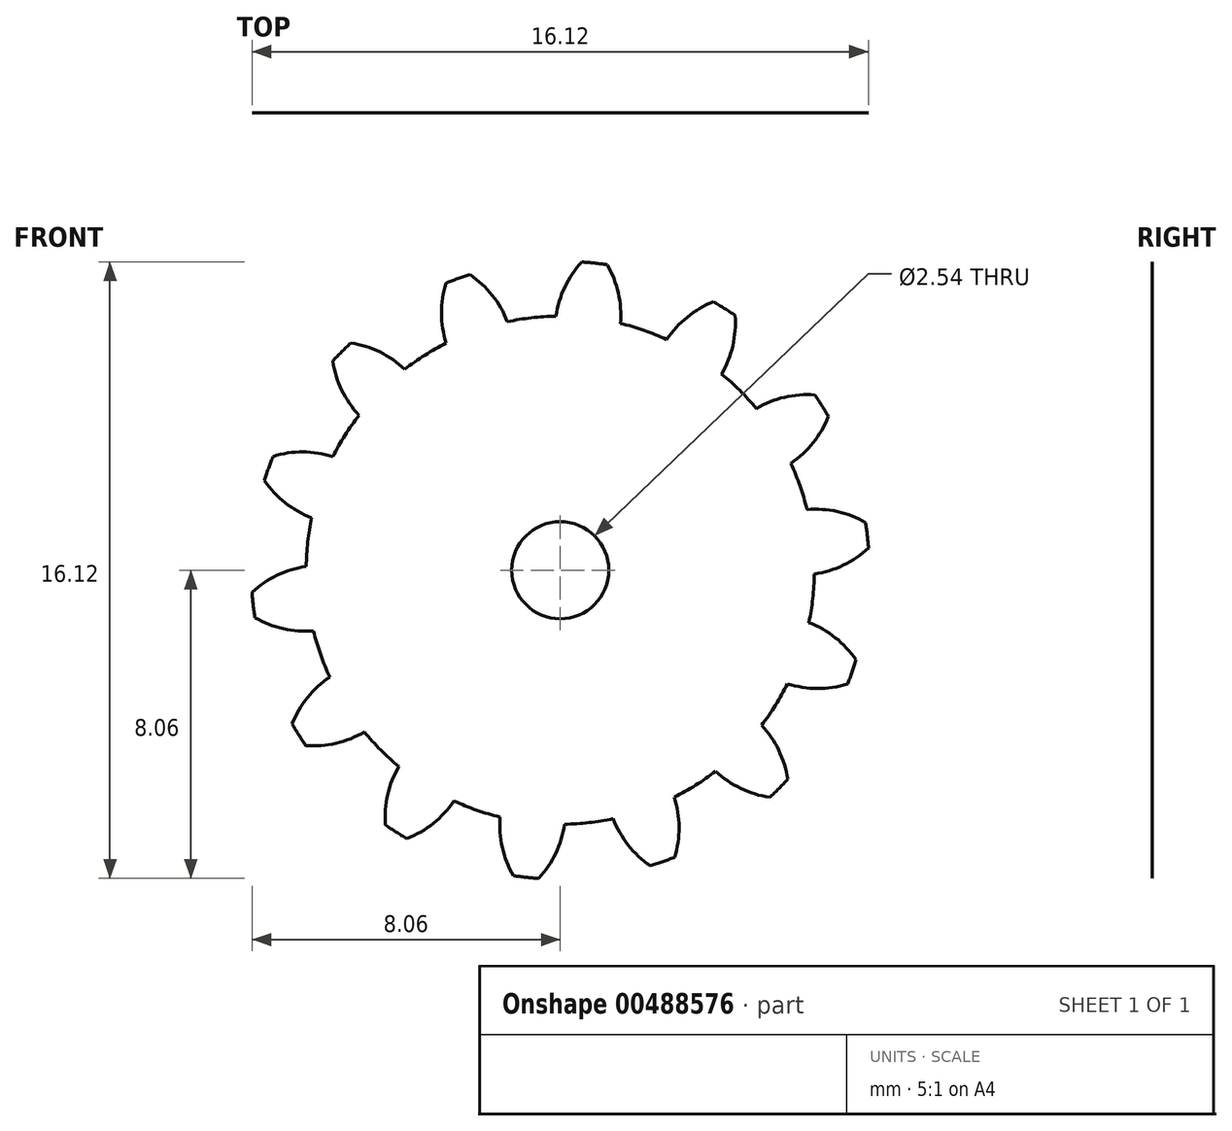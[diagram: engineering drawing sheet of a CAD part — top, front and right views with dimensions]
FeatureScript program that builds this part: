
annotation { "Feature Type Name" : "Feature", "Feature Type Description" : "" }
export const myFeature = defineFeature(function(context is Context, id is Id, definition is map)
    precondition{}
    {
        {
            assignVariable(context, id + "F0", {"name" : "teeth", "anyValue" : 14});
        }
        {
            var Q0;
            Q0=qCreatedBy(makeId("Front.planeOp"),FACE);
            var sketch = newSketch(context, id + "F1", { "sketchPlane" : qUnion([Q0])});
            skCircle(sketch, "E0", {"center": v(0, 0) * mm, "radius": 7.07 * mm, "construction": true});
            skCircle(sketch, "E1", {"center": v(0, 0) * mm, "radius": 8.08 * mm, "construction": true});
            skCircle(sketch, "E2", {"center": v(0, 0) * mm, "radius": 6.64 * mm});
            skCircle(sketch, "E3", {"center": v(14.14, 0) * mm, "radius": 6.64 * mm, "construction": true});
            skLineSegment(sketch, "E4", {"start": v(6.24, 2.27) * mm, "end": v(7.07, 0) * mm, "construction": true});
            skLineSegment(sketch, "E5", {"start": v(0, 0) * mm, "end": v(7.07, 0) * mm, "construction": true});
            skLineSegment(sketch, "E6", {"start": v(7.07, 0) * mm, "end": v(7.07, 28.46) * mm, "construction": true});
            skLineSegment(sketch, "E7", {"start": v(7.07, 0) * mm, "end": v(7.9, -2.27) * mm, "construction": true});
            skLineSegment(sketch, "E8", {"start": v(7.07, 0) * mm, "end": v(14.14, 0) * mm, "construction": true});
            skLineSegment(sketch, "E9", {"start": v(6.24, 2.27) * mm, "end": v(0, 0) * mm, "construction": true});
            skArc(sketch, "E10", {"start": v(6.24, 2.27) * mm, "mid": v(6.55, 1.1) * mm, "end": v(6.64, -0.1) * mm, "construction": true});
            skArc(sketch, "E11", {"start": v(6.64, -0.1) * mm, "mid": v(6.28, 2.16) * mm, "end": v(5.18, 4.16) * mm, "construction": true});
            skLineSegment(sketch, "E12", {"start": v(5.18, 4.16) * mm, "end": v(0, 0) * mm, "construction": true});
            skLineSegment(sketch, "E13", {"start": v(5.18, 4.16) * mm, "end": v(8.06, 0.58) * mm, "construction": true});
            skLineSegment(sketch, "E14", {"start": v(6.64, -0.1) * mm, "end": v(0, 0) * mm, "construction": true});
            skArc(sketch, "E15", {"start": v(6.64, -0.1) * mm, "mid": v(7.4, 0.13) * mm, "end": v(8.06, 0.58) * mm});
            skLineSegment(sketch, "E16", {"start": v(0, 0) * mm, "end": v(8.03, 0.91) * mm, "construction": true});
            skArc(sketch, "E17.MirrorCS", {"start": v(6.45, 1.59) * mm, "mid": v(7.24, 1.53) * mm, "end": v(7.98, 1.24) * mm});
            skPoint(sketch, "E18", {"position": v(6.89, 1.59) * mm});
            skArc(sketch, "E19", {"start": v(8.06, 0.58) * mm, "mid": v(8.03, 0.91) * mm, "end": v(7.98, 1.24) * mm});
            skPoint(sketch, "E20", {"position": v(6.6, 0.75) * mm});
            skArc(sketch, "E21", {"start": v(6.64, -0.1) * mm, "mid": v(6.6, 0.75) * mm, "end": v(6.45, 1.59) * mm});
            skCircle(sketch, "E22", {"center": v(0, 0) * mm, "radius": 1.27 * mm});
            skSolve(sketch);
        }
        {
            var Q0;
            {var subQ0=sQuery(id+"F1.wireOp",EDGE,"E2");var subQ1=makeQuery(id+"F1.imprint","INTERSECT",VERTEX,{"derivedFrom":[subQ0,sQuery(id+"F1.wireOp",EDGE,"E15")]});Q0=makeQuery(id+"F1.imprint","IMPRINT",FACE,{"disambiguationData":[TD([[makeQuery(id+"F1.imprint","IMPRINT",EDGE,{"disambiguationData":[TD([[subQ1,1.0]])],"derivedFrom":subQ0}),1.0]])]});}
            extrude(context, id + "F2", {"entities" : qUnion([Q0]), "depth" : 1 / 203.2 * mm});
        }
        {
            var Q0;
            {var subQ0=sQuery(id+"F1.wireOp",EDGE,"E15");Q0=makeQuery(id+"F1.imprint","IMPRINT",FACE,{"disambiguationData":[TD([[makeQuery(id+"F1.imprint","IMPRINT",EDGE,{"derivedFrom":subQ0}),1.0]])]});}
            extrude(context, id + "F3", {"entities" : qUnion([Q0]), "depth" : 1 / 203.2 * mm});
        }
        {
            var Q0;
            Q0=qCreatedBy(makeId("Right.planeOp"),FACE);
            var sketch = newSketch(context, id + "F4", { "sketchPlane" : qUnion([Q0])});
            skLineSegment(sketch, "E23", {"start": v(0, 0) * mm, "end": v(12.3, 0) * mm});
            skSolve(sketch);
        }
        {
            var Q0;
            Q0=makeQuery(id+"F3.opExtrude","SWEPT_BODY",BODY,{"disambiguationData":[OSD([sQuery(id+"F1.wireOp",EDGE,"E2"),sQuery(id+"F1.wireOp",EDGE,"E15"),sQuery(id+"F1.wireOp",EDGE,"E17.MirrorCS"),sQuery(id+"F1.wireOp",EDGE,"E19")])]});
            var Q1;
            Q1=sQuery(id+"F4.wireOp",EDGE,"E23");
            circularPattern(context, id + "F5", {"operationType" : NewBodyOperationType.ADD, "entities" : qUnion([Q0]), "axis" : qUnion([Q1]), "angle" : (360 / getVariable(context, 'teeth')) * degree, "instanceCount" : getVariable(context, 'teeth')});
        }
    });
